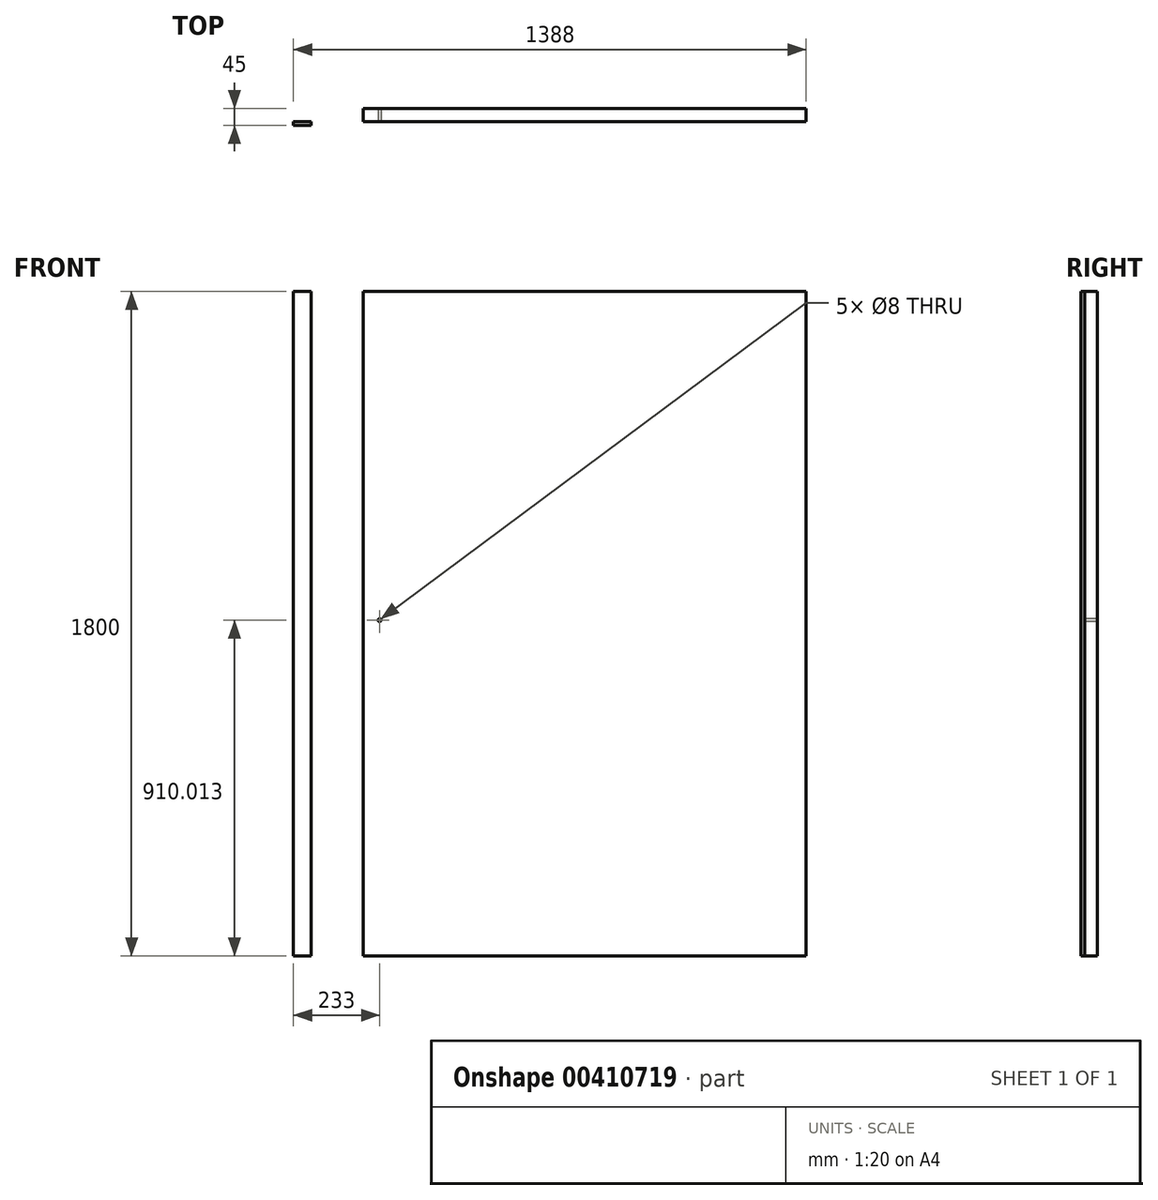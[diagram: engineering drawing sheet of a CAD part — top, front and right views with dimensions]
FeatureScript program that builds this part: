
annotation { "Feature Type Name" : "Feature", "Feature Type Description" : "" }
export const myFeature = defineFeature(function(context is Context, id is Id, definition is map)
    precondition{}
    {
        {
            var Q0;
            Q0=qCreatedBy(makeId("Front.planeOp"),FACE);
            var sketch = newSketch(context, id + "F0", { "sketchPlane" : qUnion([Q0])});
            skLineSegment(sketch, "E0.bottom", {"start": v(600, 900) * mm, "end": v(-600, 900) * mm});
            skLineSegment(sketch, "E0.top", {"start": v(600, -900) * mm, "end": v(-600, -900) * mm});
            skLineSegment(sketch, "E0.left", {"start": v(600, 900) * mm, "end": v(600, -900) * mm});
            skLineSegment(sketch, "E0.right", {"start": v(-600, 900) * mm, "end": v(-600, -900) * mm});
            skPoint(sketch, "E0.middle", {"position": v(0, 0) * mm});
            skSolve(sketch);
        }
        {
            var Q0;
            Q0=makeQuery(id+"F0.imprint","IMPRINT",FACE,{"disambiguationData":[TD([[makeQuery(id+"F0.imprint","IMPRINT",EDGE,{"derivedFrom":sQuery(id+"F0.wireOp",EDGE,"E0.bottom")}),1.0]])]});
            extrude(context, id + "F1", {"entities" : qUnion([Q0]), "oppositeDirection" : true, "depth" : 35 * mm});
        }
        {
            var Q0;
            Q0=makeQuery(id+"F1.opExtrude","CAP_FACE",FACE,{"disambiguationData":[OSD([sQuery(id+"F0.wireOp",EDGE,"E0.bottom"),sQuery(id+"F0.wireOp",EDGE,"E0.top"),sQuery(id+"F0.wireOp",EDGE,"E0.left"),sQuery(id+"F0.wireOp",EDGE,"E0.right")])],"isStart":true});
            var sketch = newSketch(context, id + "F2", { "sketchPlane" : qUnion([Q0])});
            skCircle(sketch, "E1", {"center": v(-555, 10.01) * mm, "radius": 4 * mm});
            skSolve(sketch);
        }
        {
            var Q0;
            Q0 = qSketchRegion(id + "F2", true);
            extrude(context, id + "F3", {"entities" : qUnion([Q0]), "operationType" : NewBodyOperationType.REMOVE, "endBound" : BoundingType.THROUGH_ALL, "oppositeDirection" : true, "depth" : 25 * mm});
        }
        {
            var Q0;
            Q0=qCreatedBy(makeId("Front.planeOp"),FACE);
            var sketch = newSketch(context, id + "F4", { "sketchPlane" : qUnion([Q0])});
            skLineSegment(sketch, "E2.bottom", {"start": v(-740.5, 900) * mm, "end": v(-788, 900) * mm});
            skLineSegment(sketch, "E2.top", {"start": v(-740.5, -900) * mm, "end": v(-788, -900) * mm});
            skLineSegment(sketch, "E2.left", {"start": v(-740.5, 900) * mm, "end": v(-740.5, -900) * mm});
            skLineSegment(sketch, "E2.right", {"start": v(-788, 900) * mm, "end": v(-788, -900) * mm});
            skPoint(sketch, "E2.middle", {"position": v(-764.25, 0) * mm});
            skSolve(sketch);
        }
        {
            var Q0;
            Q0=makeQuery(id+"F4.imprint","IMPRINT",FACE,{"disambiguationData":[TD([[makeQuery(id+"F4.imprint","IMPRINT",EDGE,{"derivedFrom":sQuery(id+"F4.wireOp",EDGE,"E2.bottom")}),1.0]])]});
            extrude(context, id + "F5", {"entities" : qUnion([Q0]), "depth" : 10 * mm});
        }
    });
